# Revit family: CWP
name_source: partatom
category: Lighting Fixtures
units: mm (PartAtom-declared; Revit-internal decimal feet)

## family parameters
Cut with Voids When Loaded = No
Host = Face
Light Source = Yes
OmniClass Number = 23.80.70.11
OmniClass Title = Luminaries for Internal Lighting
Part Type = Normal
Room Calculation Point = No
Round Connector Dimension = Use Diameter
Shared = No

## types (2) — shared parameters
Apparent Load = 37 VA
Backbox = White
Color Filter = 16777215
Default Elevation = 4.00'
Description = Wrap Luminaire
Dimming = 0-10V
Dimming Lamp Color Temperature Shift = <None>
Emit Shape Visible in Rendering = No
Emit from Rectangle Length = 3.92'
Emit from Rectangle Width = 0.67'
Glass = White Glass
Lamp = LED Lamp
Load Classification = Lighting
Manufacturer = Columbia Lighting
Model = CWP4
Photometric Web File = generic.ies
Power Factor = 1
Row Length = 4.00'
Tilt Angle = -90.00°
URL = https://www.currentlighting.com
Voltage = 120 V
Warranty = Five Year Warranty
Wattage Comments = Up to 124 lumens per watt
Watts = 37 W

## type names (no varying parameters)
- CWP4-4035
- CWP4-4040

## geometry (parser evidence)
native form markers: Blend x4, Sweep x5
no freeform markers — native parametric forms only
